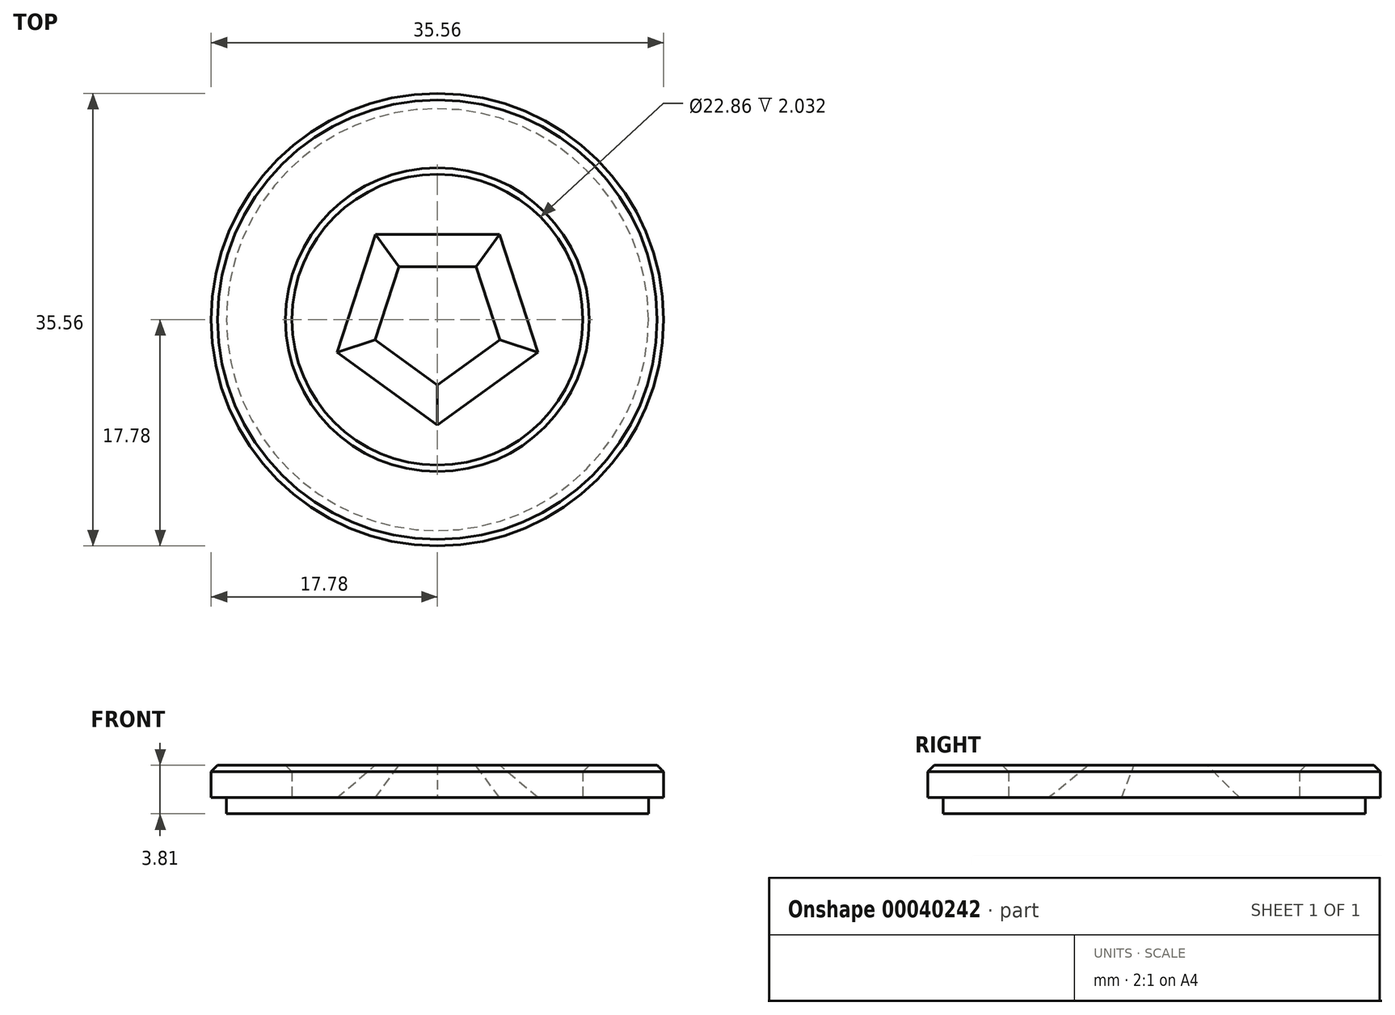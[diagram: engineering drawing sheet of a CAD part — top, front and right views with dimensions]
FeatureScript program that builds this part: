
annotation { "Feature Type Name" : "Feature", "Feature Type Description" : "" }
export const myFeature = defineFeature(function(context is Context, id is Id, definition is map)
    precondition{}
    {
        {
            var Q0;
            Q0=qCreatedBy(makeId("Top.planeOp"),FACE);
            var sketch = newSketch(context, id + "F0", { "sketchPlane" : qUnion([Q0])});
            skCircle(sketch, "E0", {"center": v(0, 0) * mm, "radius": 17.78 * mm});
            skCircle(sketch, "E1", {"center": v(0, 0) * mm, "radius": 11.43 * mm});
            skCircle(sketch, "E2.cCircle", {"center": v(0, 0) * mm, "radius": 9.25 * mm, "construction": true});
            skLineSegment(sketch, "E2.0", {"start": v(-6.72, 9.25) * mm, "end": v(6.72, 9.25) * mm});
            skLineSegment(sketch, "E2.1", {"start": v(6.72, 9.25) * mm, "end": v(10.87, -3.53) * mm});
            skLineSegment(sketch, "E2.2", {"start": v(10.87, -3.53) * mm, "end": v(0, -11.43) * mm});
            skLineSegment(sketch, "E2.3", {"start": v(0, -11.43) * mm, "end": v(-10.87, -3.53) * mm});
            skLineSegment(sketch, "E2.4", {"start": v(-10.87, -3.53) * mm, "end": v(-6.72, 9.25) * mm});
            skPoint(sketch, "E2.0.midPoint", {"position": v(0, 9.25) * mm});
            skSolve(sketch);
        }
        {
            var Q0;
            Q0 = qSketchRegion(id + "F0", true);
            var Q1;
            Q1=makeQuery(id+"F0.imprint","IMPRINT",FACE,{"disambiguationData":[TD([[makeQuery(id+"F0.imprint","IMPRINT",EDGE,{"derivedFrom":sQuery(id+"F0.wireOp",EDGE,"E2.0")}),-1.0]])]});
            extrude(context, id + "F1", {"entities" : qUnion([Q0, Q1]), "depth" : 2.54 * mm});
        }
        {
            var Q0;
            Q0=makeQuery(id+"F1.opExtrude","CAP_FACE",FACE,{"disambiguationData":[OSD([sQuery(id+"F0.wireOp",EDGE,"E0"),sQuery(id+"F0.wireOp",EDGE,"E1")])],"isStart":false});
            chamfer(context, id + "F2", {"entities" : qUnion([Q0]), "width" : 0.5 * mm, "tangentPropagation" : true});
        }
        {
            var Q0;
            Q0=makeQuery(id+"F1.opExtrude","CAP_FACE",FACE,{"disambiguationData":[OSD([sQuery(id+"F0.wireOp",EDGE,"E2.0"),sQuery(id+"F0.wireOp",EDGE,"E2.1"),sQuery(id+"F0.wireOp",EDGE,"E2.2"),sQuery(id+"F0.wireOp",EDGE,"E2.3"),sQuery(id+"F0.wireOp",EDGE,"E2.4")])],"isStart":false});
            chamfer(context, id + "F3", {"entities" : qUnion([Q0]), "width" : 5.08 * mm, "tangentPropagation" : true});
        }
        {
            var Q0;
            Q0=qCreatedBy(makeId("Top.planeOp"),FACE);
            var sketch = newSketch(context, id + "F4", { "sketchPlane" : qUnion([Q0])});
            skCircle(sketch, "E3", {"center": v(0, 0) * mm, "radius": 16.58 * mm});
            skSolve(sketch);
        }
        {
            var Q0;
            Q0 = qSketchRegion(id + "F4", true);
            extrude(context, id + "F5", {"entities" : qUnion([Q0]), "oppositeDirection" : true, "depth" : 1.27 * mm});
        }
    });
